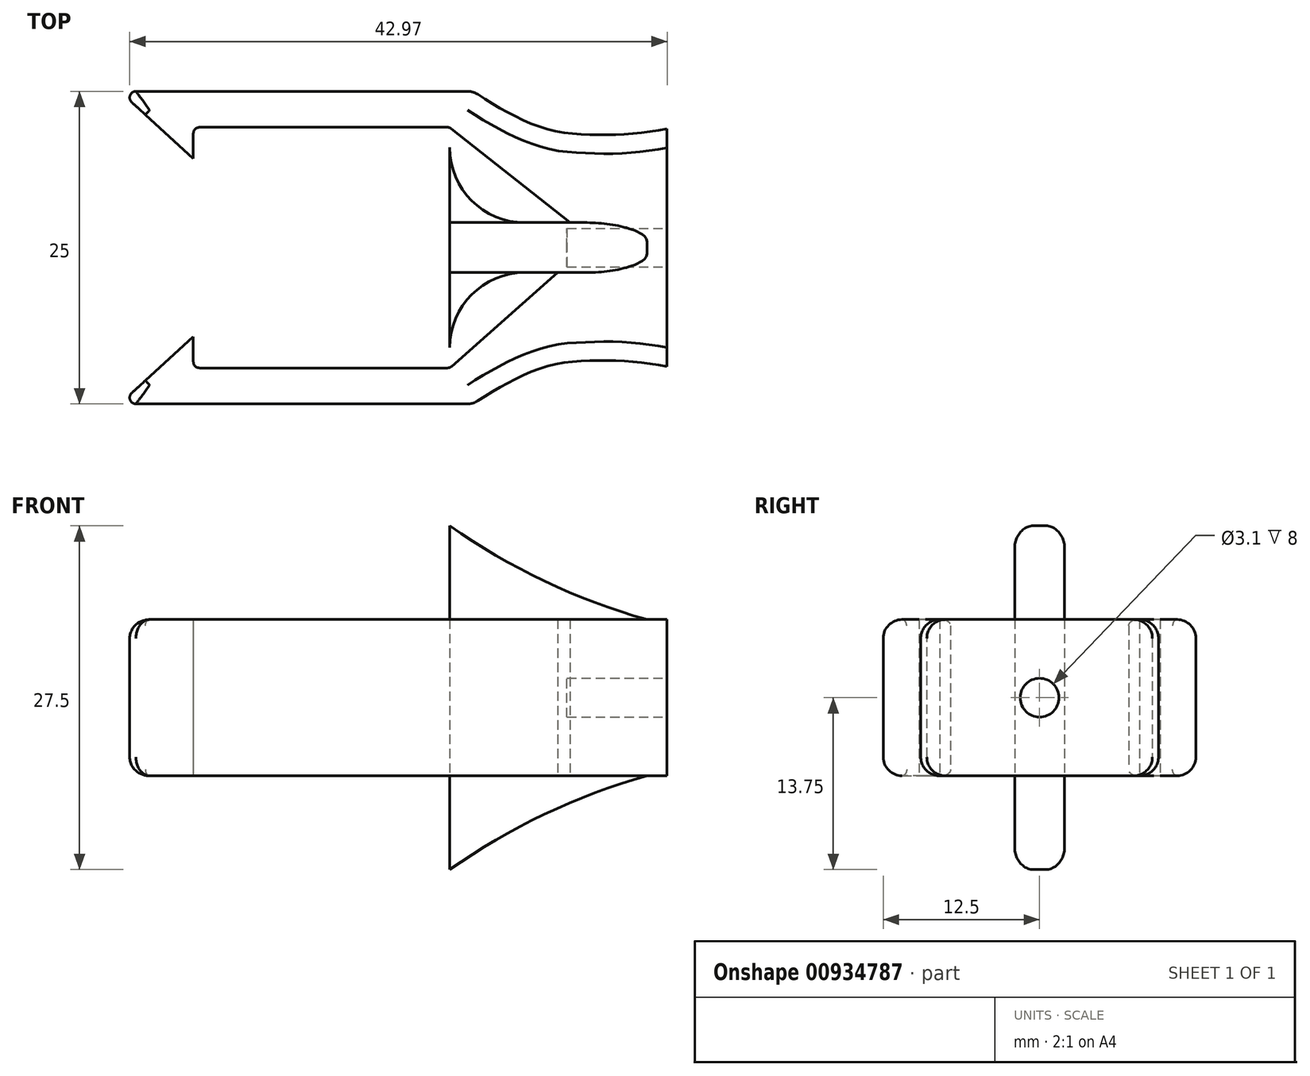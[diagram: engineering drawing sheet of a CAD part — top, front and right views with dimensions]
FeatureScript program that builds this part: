
annotation { "Feature Type Name" : "Feature", "Feature Type Description" : "" }
export const myFeature = defineFeature(function(context is Context, id is Id, definition is map)
    precondition{}
    {
        {
            var Q0;
            Q0=qCreatedBy(makeId("Top.planeOp"),FACE);
            var sketch = newSketch(context, id + "F0", { "sketchPlane" : qUnion([Q0])});
            skLineSegment(sketch, "E0.bottom", {"start": v(10.25, -9.62) * mm, "end": v(-10.25, -9.63) * mm});
            skLineSegment(sketch, "E0.top", {"start": v(10.25, 9.63) * mm, "end": v(-10.25, 9.62) * mm});
            skLineSegment(sketch, "E0.right", {"start": v(-10.25, -9.63) * mm, "end": v(-10.25, -7.12) * mm});
            skPoint(sketch, "E0.middle", {"position": v(0, 0) * mm});
            skLineSegment(sketch, "E1.bottom", {"start": v(12.12, -12.5) * mm, "end": v(-12.12, -12.5) * mm});
            skLineSegment(sketch, "E1.top", {"start": v(12.12, 12.5) * mm, "end": v(-12.12, 12.5) * mm});
            skLineSegment(sketch, "E2", {"start": v(-12.12, 12.5) * mm, "end": v(-16.12, 12.5) * mm});
            skLineSegment(sketch, "E3", {"start": v(-16.13, 12.5) * mm, "end": v(-10.25, 7.12) * mm});
            skLineSegment(sketch, "E4", {"start": v(-10.25, 7.12) * mm, "end": v(-10.25, 9.62) * mm});
            skLineSegment(sketch, "E5.MirrorCS", {"start": v(-16.12, -12.5) * mm, "end": v(-10.25, -7.13) * mm});
            skLineSegment(sketch, "E6.MirrorCS", {"start": v(-10.25, -7.13) * mm, "end": v(-10.25, -11.12) * mm});
            skLineSegment(sketch, "E7", {"start": v(-12.12, -12.5) * mm, "end": v(-16.12, -12.5) * mm});
            skLineSegment(sketch, "E8.left", {"start": v(27.62, 9.5) * mm, "end": v(27.62, -9.5) * mm});
            skFitSpline(sketch, "E9", {"points": [v(12.12, 12.5) * mm, v(21.1, 9.06) * mm, v(27.62, 9.5) * mm], "startDerivative": vector(27.3, -18.19) * mm, "endDerivative": vector(22.46, 3.99) * mm});
            skFitSpline(sketch, "E10.MirrorCS", {"points": [v(12.12, -12.5) * mm, v(21.1, -9.06) * mm, v(27.62, -9.5) * mm], "startDerivative": vector(27.3, 18.19) * mm, "endDerivative": vector(22.46, -3.99) * mm});
            skLineSegment(sketch, "E11.0", {"start": v(27.62, -2) * mm, "end": v(16.25, -2) * mm});
            skLineSegment(sketch, "E12", {"start": v(19.88, 2) * mm, "end": v(10.25, 9.63) * mm});
            skLineSegment(sketch, "E13", {"start": v(18.89, -2) * mm, "end": v(10.25, -9.63) * mm});
            skLineSegment(sketch, "E14", {"start": v(10.25, -8) * mm, "end": v(10.25, -7.83) * mm});
            skPoint(sketch, "E15.newPointA", {"position": v(10.25, 0) * mm});
            skPoint(sketch, "E15.newPointB", {"position": v(10.15, -2) * mm});
            skArc(sketch, "E15.filletArc", {"start": v(16.25, -2) * mm, "mid": v(12, -3.76) * mm, "end": v(10.25, -8) * mm});
            skLineSegment(sketch, "E16", {"start": v(10.25, -8) * mm, "end": v(10.25, 0) * mm});
            skLineSegment(sketch, "E17", {"start": v(0, 0) * mm, "end": v(28.96, 0) * mm});
            skPoint(sketch, "E17.endSnap0", {"position": v(27.62, 0) * mm});
            skLineSegment(sketch, "E18.MirrorCS", {"start": v(10.25, 8) * mm, "end": v(10.25, 0) * mm});
            skArc(sketch, "E19.MirrorCS", {"start": v(16.25, 2) * mm, "mid": v(12, 3.76) * mm, "end": v(10.25, 8) * mm});
            skLineSegment(sketch, "E20.MirrorCS", {"start": v(27.62, 2) * mm, "end": v(16.25, 2) * mm});
            skSolve(sketch);
        }
        {
            var Q0;
            Q0=qSketchRegion(id+"F0",true);
            extrude(context, id + "F1", {"entities" : qUnion([Q0]), "endBound" : BoundingType.SYMMETRIC, "depth" : 12.5 * mm, "offsetDistance" : 25 * mm});
        }
        {
            var Q0;
            Q0=qCreatedBy(makeId("Front.planeOp"),FACE);
            var sketch = newSketch(context, id + "F2", { "sketchPlane" : qUnion([Q0])});
            skLineSegment(sketch, "E21", {"start": v(10.25, 6.25) * mm, "end": v(10.25, 13.75) * mm});
            skArc(sketch, "E22", {"start": v(10.25, 13.75) * mm, "mid": v(18.29, 9.11) * mm, "end": v(27.02, 5.98) * mm});
            skLineSegment(sketch, "E23", {"start": v(10.25, 6.25) * mm, "end": v(27.02, 5.98) * mm});
            skLineSegment(sketch, "E24.MirrorCS", {"start": v(10.25, -6.25) * mm, "end": v(27.02, -5.98) * mm});
            skLineSegment(sketch, "E25.MirrorCS", {"start": v(10.25, -6.25) * mm, "end": v(10.25, -13.75) * mm});
            skArc(sketch, "E26.MirrorCS", {"start": v(10.25, -13.75) * mm, "mid": v(18.29, -9.11) * mm, "end": v(27.02, -5.98) * mm});
            skSolve(sketch);
        }
        {
            var Q0;
            Q0=qSketchRegion(id+"F2",true);
            extrude(context, id + "F3", {"entities" : qUnion([Q0]), "operationType" : NewBodyOperationType.ADD, "endBound" : BoundingType.SYMMETRIC, "depth" : 4 * mm, "offsetDistance" : 25 * mm});
        }
        {
            var Q0;
            Q0=makeQuery(id+"F1.opExtrude","CAP_EDGE",EDGE,{"disambiguationData":[OSD([sQuery(id+"F0.wireOp",EDGE,"E1.top"),sQuery(id+"F0.wireOp",EDGE,"E2")])],"isStart":false});
            var Q1;
            Q1=makeQuery(id+"F1.opExtrude","CAP_EDGE",EDGE,{"disambiguationData":[OSD([sQuery(id+"F0.wireOp",EDGE,"E1.top"),sQuery(id+"F0.wireOp",EDGE,"E2")])],"isStart":true});
            var Q2;
            Q2=makeQuery(id+"F1.opExtrude","CAP_EDGE",EDGE,{"disambiguationData":[OSD([sQuery(id+"F0.wireOp",EDGE,"E1.bottom"),sQuery(id+"F0.wireOp",EDGE,"E7")])],"isStart":true});
            var Q3;
            Q3=makeQuery(id+"F1.opExtrude","CAP_EDGE",EDGE,{"disambiguationData":[OSD([sQuery(id+"F0.wireOp",EDGE,"E1.bottom"),sQuery(id+"F0.wireOp",EDGE,"E7")])],"isStart":false});
            var Q4;
            Q4=makeQuery(id+"F1.opExtrude","SWEPT_EDGE",EDGE,{"disambiguationData":[OSD([sQuery(id+"F0.wireOp",EDGE,"E1.bottom"),sQuery(id+"F0.wireOp",EDGE,"E1.left"),sQuery(id+"F0.wireOp",EDGE,"E10.MirrorCS"),sQuery(id+"F0.wireOp",EDGE,"6qCA9TG6-yP8q-QHqZ-n07t-xfMhLHNTlp1A")])]});
            var Q5;
            Q5=makeQuery(id+"F1.opExtrude","CAP_EDGE",EDGE,{"disambiguationData":[OSD([sQuery(id+"F0.wireOp",EDGE,"E10.MirrorCS")])],"isStart":true});
            var Q6;
            Q6=makeQuery(id+"F1.opExtrude","CAP_EDGE",EDGE,{"disambiguationData":[OSD([sQuery(id+"F0.wireOp",EDGE,"E10.MirrorCS")])],"isStart":false});
            var Q7;
            Q7=makeQuery(id+"F1.opExtrude","CAP_EDGE",EDGE,{"disambiguationData":[OSD([sQuery(id+"F0.wireOp",EDGE,"E9")])],"isStart":true});
            var Q8;
            Q8=makeQuery(id+"F1.opExtrude","CAP_EDGE",EDGE,{"disambiguationData":[OSD([sQuery(id+"F0.wireOp",EDGE,"E9")])],"isStart":false});
            var Q9;
            Q9=makeQuery(id+"F1.opExtrude","SWEPT_EDGE",EDGE,{"disambiguationData":[OSD([sQuery(id+"F0.wireOp",EDGE,"E1.top"),sQuery(id+"F0.wireOp",EDGE,"E1.left"),sQuery(id+"F0.wireOp",EDGE,"E9"),sQuery(id+"F0.wireOp",EDGE,"Nb5HneMs-bZkN-5T6f-8Fwy-dr1VcnucefEy")])]});
            var Q10;
            Q10=makeQuery(id+"F3.opExtrude","CAP_EDGE",EDGE,{"disambiguationData":[OSD([sQuery(id+"F2.wireOp",EDGE,"E22")])],"isStart":false});
            var Q11;
            Q11=makeQuery(id+"F3.opExtrude","CAP_EDGE",EDGE,{"disambiguationData":[OSD([sQuery(id+"F2.wireOp",EDGE,"E22")])],"isStart":true});
            var Q12;
            Q12=makeQuery(id+"F3.opExtrude","CAP_EDGE",EDGE,{"disambiguationData":[OSD([sQuery(id+"F2.wireOp",EDGE,"E26.MirrorCS")])],"isStart":false});
            var Q13;
            Q13=makeQuery(id+"F3.opExtrude","CAP_EDGE",EDGE,{"disambiguationData":[OSD([sQuery(id+"F2.wireOp",EDGE,"E26.MirrorCS")])],"isStart":true});
            fillet(context, id + "F4", {"entities" : qUnion([Q0, Q1, Q2, Q3, Q4, Q5, Q6, Q7, Q8, Q9, Q10, Q11, Q12, Q13]), "radius" : 1.5 * mm, "tangentPropagation" : true, "allowEdgeOverflow" : false});
        }
        {
            var Q0;
            Q0=makeQuery(id+"F1.opExtrude","SWEPT_EDGE",EDGE,{"disambiguationData":[OSD([sQuery(id+"F0.wireOp",EDGE,"E0.top"),sQuery(id+"F0.wireOp",EDGE,"E0.left")])]});
            var Q1;
            Q1=makeQuery(id+"F1.opExtrude","SWEPT_EDGE",EDGE,{"disambiguationData":[OSD([sQuery(id+"F0.wireOp",EDGE,"E0.bottom"),sQuery(id+"F0.wireOp",EDGE,"E0.left")])]});
            var Q2;
            Q2=makeQuery(id+"F1.opExtrude","SWEPT_EDGE",EDGE,{"disambiguationData":[OSD([sQuery(id+"F0.wireOp",EDGE,"E2"),sQuery(id+"F0.wireOp",EDGE,"E3")])]});
            var Q3;
            Q3=makeQuery(id+"F1.opExtrude","SWEPT_EDGE",EDGE,{"disambiguationData":[OSD([sQuery(id+"F0.wireOp",EDGE,"E5.MirrorCS"),sQuery(id+"F0.wireOp",EDGE,"E7")])]});
            fillet(context, id + "F5", {"entities" : qUnion([Q0, Q1, Q2, Q3]), "radius" : .5 * mm, "tangentPropagation" : true, "allowEdgeOverflow" : false});
        }
        {
            var Q0;
            Q0=makeQuery(id+"F1.opExtrude","SWEPT_FACE",FACE,{"disambiguationData":[OSD([sQuery(id+"F0.wireOp",EDGE,"E8.left")])]});
            var sketch = newSketch(context, id + "F6", { "sketchPlane" : qUnion([Q0])});
            skCircle(sketch, "E27", {"center": v(0, 0) * mm, "radius": 1.55 * mm});
            skSolve(sketch);
        }
        {
            var Q0;
            Q0 = qSketchRegion(id + "F6", true);
            extrude(context, id + "F7", {"entities" : qUnion([Q0]), "operationType" : NewBodyOperationType.REMOVE, "oppositeDirection" : true, "depth" : 8 * mm, "offsetDistance" : 25 * mm});
        }
    });
